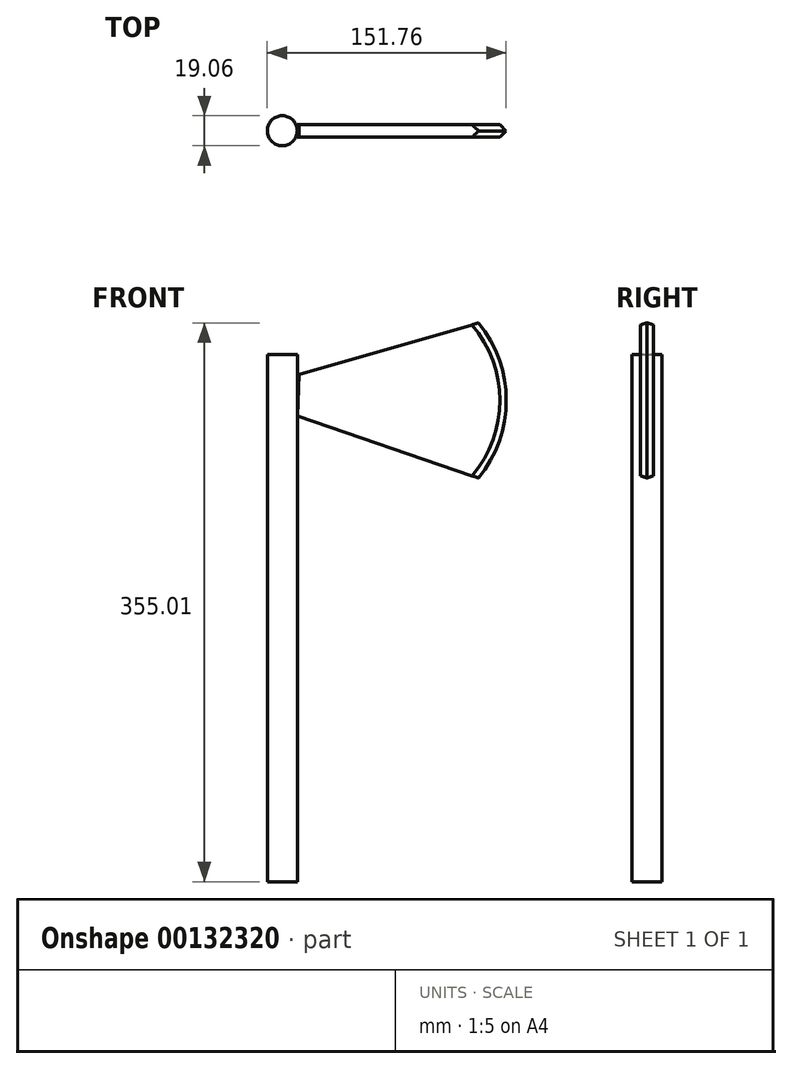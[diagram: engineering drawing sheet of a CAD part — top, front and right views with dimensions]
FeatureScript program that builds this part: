
annotation { "Feature Type Name" : "Feature", "Feature Type Description" : "" }
export const myFeature = defineFeature(function(context is Context, id is Id, definition is map)
    precondition{}
    {
        {
            var Q0;
            Q0=qCreatedBy(makeId("Top.planeOp"),FACE);
            var sketch = newSketch(context, id + "F0", { "sketchPlane" : qUnion([Q0])});
            skCircle(sketch, "E0", {"center": v(0, 0) * mm, "radius": 9.53 * mm});
            skSolve(sketch);
        }
        {
            var Q0;
            Q0=makeQuery(id+"F0.imprint","IMPRINT",FACE,{"disambiguationData":[TD([[makeQuery(id+"F0.imprint","IMPRINT",EDGE,{"derivedFrom":sQuery(id+"F0.wireOp",EDGE,"E0")}),1.0]])]});
            extrude(context, id + "F1", {"entities" : qUnion([Q0]), "depth" : 334.85 * mm});
        }
        {
            var Q0;
            Q0=qCreatedBy(makeId("Front.planeOp"),FACE);
            var sketch = newSketch(context, id + "F2", { "sketchPlane" : qUnion([Q0])});
            skLineSegment(sketch, "E1", {"start": v(10.66, 322.32) * mm, "end": v(125.75, 355.3) * mm});
            skLineSegment(sketch, "E2", {"start": v(9.81, 295.75) * mm, "end": v(125.75, 256.13) * mm});
            skLineSegment(sketch, "E3", {"start": v(10.66, 322.32) * mm, "end": v(9.81, 295.75) * mm});
            skArc(sketch, "E4", {"start": v(125.75, 256.13) * mm, "mid": v(143.23, 305.72) * mm, "end": v(125.75, 355.3) * mm});
            skSolve(sketch);
        }
        {
            var Q0;
            Q0=makeQuery(id+"F2.imprint","IMPRINT",FACE,{"disambiguationData":[TD([[makeQuery(id+"F2.imprint","IMPRINT",EDGE,{"derivedFrom":sQuery(id+"F2.wireOp",EDGE,"E1")}),-1.0]])]});
            extrude(context, id + "F3", {"entities" : qUnion([Q0]), "depth" : 4.18 * mm, "hasSecondDirection" : true, "secondDirectionOppositeDirection" : true, "secondDirectionDepth" : 4 * mm});
        }
        {
            var Q0;
            Q0=makeQuery(id+"F3.opExtrude","CAP_EDGE",EDGE,{"disambiguationData":[OSD([sQuery(id+"F2.wireOp",EDGE,"E4")])],"isStart":false});
            var Q1;
            Q1=makeQuery(id+"F3.opExtrude","CAP_EDGE",EDGE,{"disambiguationData":[OSD([sQuery(id+"F2.wireOp",EDGE,"E4")])],"isStart":true});
            chamfer(context, id + "F4", {"entities" : qUnion([Q0, Q1]), "width" : 5.08 * mm, "tangentPropagation" : true});
        }
    });
